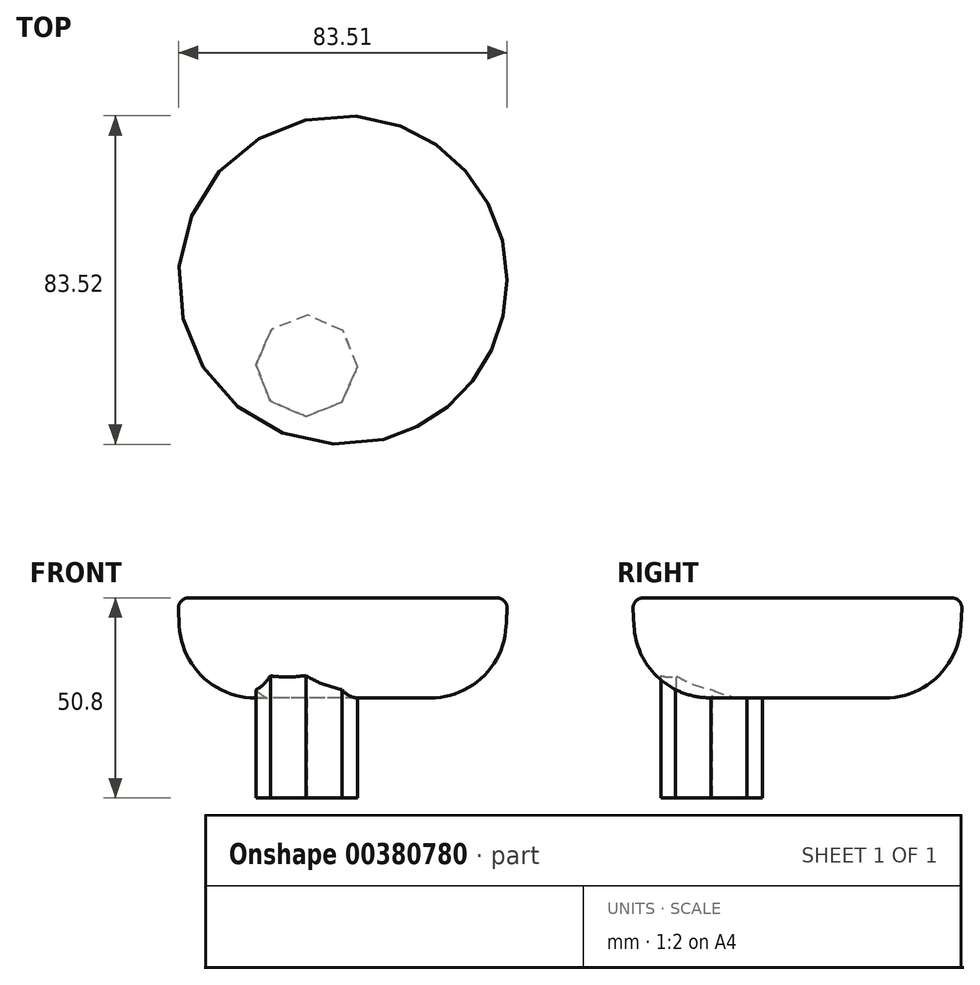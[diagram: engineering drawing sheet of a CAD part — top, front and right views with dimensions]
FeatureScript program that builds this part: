
annotation { "Feature Type Name" : "Feature", "Feature Type Description" : "" }
export const myFeature = defineFeature(function(context is Context, id is Id, definition is map)
    precondition{}
    {
        {
            var Q0;
            Q0=qCreatedBy(makeId("Top.planeOp"),FACE);
            var sketch = newSketch(context, id + "F0", { "sketchPlane" : qUnion([Q0])});
            skCircle(sketch, "E0", {"center": v(-84.22, 32.73) * mm, "radius": 40.56 * mm});
            skSolve(sketch);
        }
        {
            var Q0;
            Q0=makeQuery(id+"F0.imprint","IMPRINT",FACE,{"disambiguationData":[TD([[makeQuery(id+"F0.imprint","IMPRINT",EDGE,{"derivedFrom":sQuery(id+"F0.wireOp",EDGE,"E0")}),1.0]])]});
            extrude(context, id + "F1", {"entities" : qUnion([Q0]), "depth" : 25.4 * mm, "hasDraft" : true, "draftAngle" : 3 * degree});
        }
        {
            var Q0;
            Q0=makeQuery(id+"F1.opExtrude","CAP_EDGE",EDGE,{"disambiguationData":[OSD([sQuery(id+"F0.wireOp",EDGE,"E0")])],"isStart":false});
            fillet(context, id + "F2", {"entities" : qUnion([Q0]), "radius" : 2.54 * mm, "tangentPropagation" : true, "allowEdgeOverflow" : false});
        }
        {
            var Q0;
            Q0=makeQuery(id+"F1.opExtrude","CAP_FACE",FACE,{"disambiguationData":[OSD([sQuery(id+"F0.wireOp",EDGE,"E0")])],"isStart":true});
            var sketch = newSketch(context, id + "F3", { "sketchPlane" : qUnion([Q0])});
            skCircle(sketch, "E1.cCircle", {"center": v(-93.38, -10.94) * mm, "radius": 11.9 * mm, "construction": true});
            skLineSegment(sketch, "E1.0", {"start": v(-80.5, -10.75) * mm, "end": v(-84.13, -19.91) * mm});
            skLineSegment(sketch, "E1.1", {"start": v(-84.13, -19.91) * mm, "end": v(-93.19, -23.82) * mm});
            skLineSegment(sketch, "E1.2", {"start": v(-93.19, -23.82) * mm, "end": v(-102.35, -20.18) * mm});
            skLineSegment(sketch, "E1.3", {"start": v(-102.35, -20.18) * mm, "end": v(-106.26, -11.13) * mm});
            skLineSegment(sketch, "E1.4", {"start": v(-106.26, -11.13) * mm, "end": v(-102.62, -1.96) * mm});
            skLineSegment(sketch, "E1.5", {"start": v(-102.62, -1.96) * mm, "end": v(-93.56, 1.94) * mm});
            skLineSegment(sketch, "E1.6", {"start": v(-93.56, 1.94) * mm, "end": v(-84.4, -1.7) * mm});
            skLineSegment(sketch, "E1.7", {"start": v(-84.4, -1.7) * mm, "end": v(-80.5, -10.75) * mm});
            skPoint(sketch, "E1.0.midPoint", {"position": v(-82.31, -15.33) * mm});
            skSolve(sketch);
        }
        {
            var Q0;
            Q0=makeQuery(id+"F3.imprint","IMPRINT",FACE,{"disambiguationData":[TD([[makeQuery(id+"F3.imprint","IMPRINT",EDGE,{"derivedFrom":sQuery(id+"F3.wireOp",EDGE,"E1.0")}),-1.0]])]});
            extrude(context, id + "F4", {"entities" : qUnion([Q0]), "operationType" : NewBodyOperationType.ADD, "depth" : 25.4 * mm});
        }
        {
            var Q0;
            Q0=makeQuery(id+"F1.opExtrude","CAP_EDGE",EDGE,{"disambiguationData":[OSD([sQuery(id+"F0.wireOp",EDGE,"E0")])],"isStart":true});
            fillet(context, id + "F5", {"entities" : qUnion([Q0]), "radius" : 19.3 * mm, "tangentPropagation" : true, "allowEdgeOverflow" : false});
        }
    });
